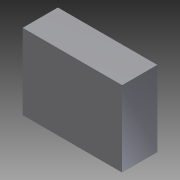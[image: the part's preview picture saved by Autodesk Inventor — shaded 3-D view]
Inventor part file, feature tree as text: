
AUTODESK INVENTOR PART (.ipt)
format: ipt  version: 2011 (Build 150239000, 239)  size: 69,120 bytes
history: native  units: in
note: dims shown in document units (in); Inventor stores cm internally (conversion verified against a paired STEP export)
features: extrude x1, sketch x1
ambient origin geometry x8: Origin, YZ Plane, XZ Plane, XY Plane, X Axis, Y Axis, Z Axis, Center Point
bodies: Solid1 (feature_tree)
feature tree (2):
  extrude  "Extrusion1"  Depth=0.1693in
  sketch  "Sketch1"  dims[d0=0.2283in d1=0.1693in d2=0.4449in d3=0.3386in d4=0.1575in d5=0.0in]
